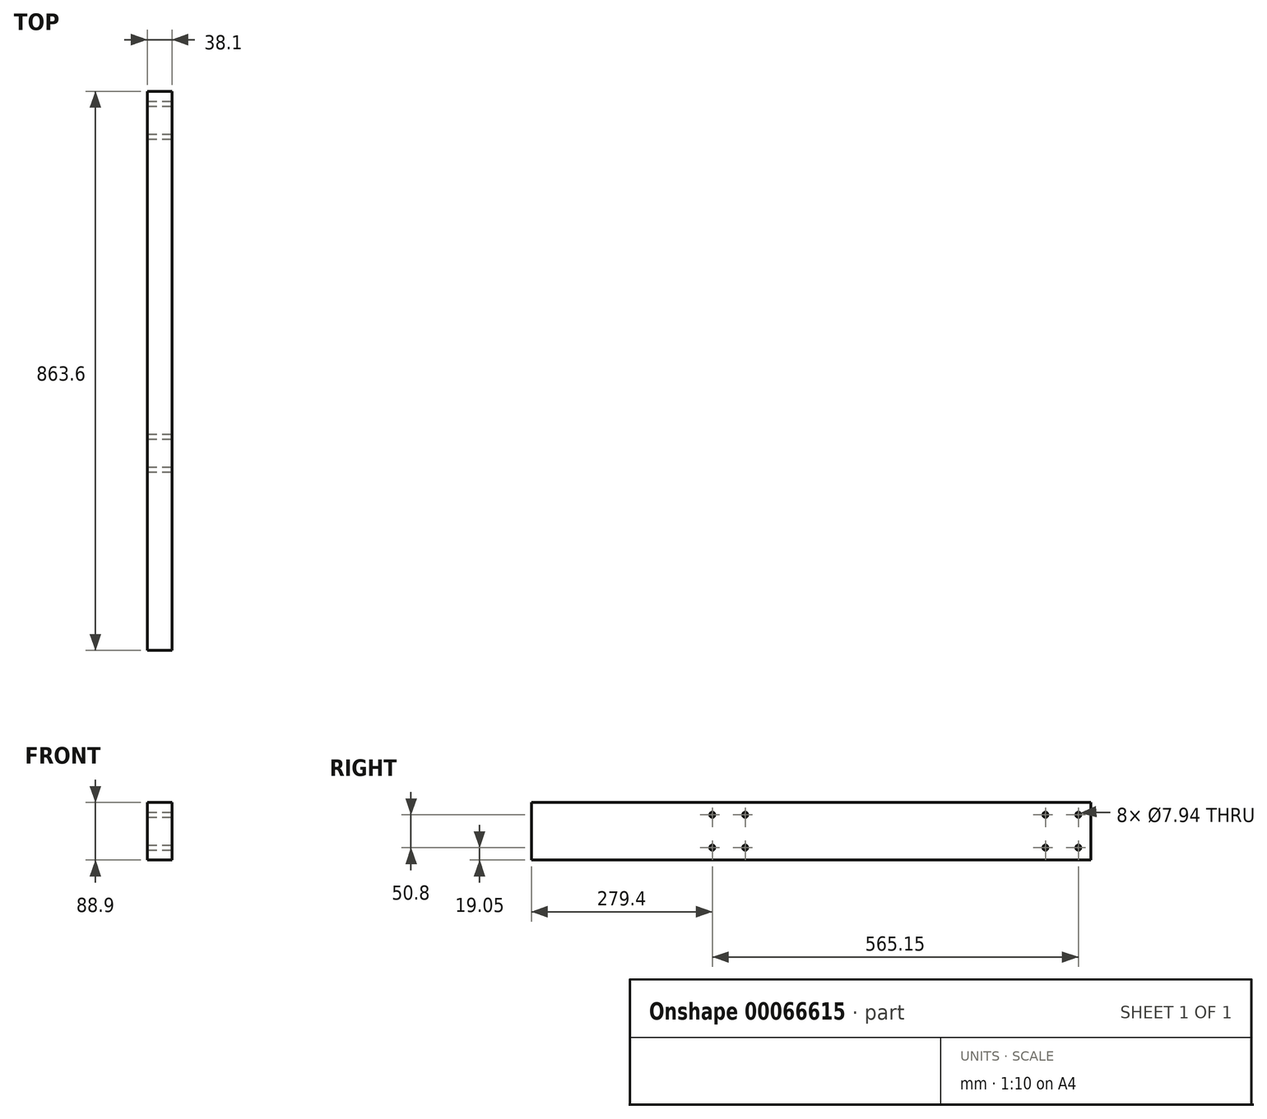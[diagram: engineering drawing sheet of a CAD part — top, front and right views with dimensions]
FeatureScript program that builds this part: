
annotation { "Feature Type Name" : "Feature", "Feature Type Description" : "" }
export const myFeature = defineFeature(function(context is Context, id is Id, definition is map)
    precondition{}
    {
        {
            var Q0;
            Q0=qCreatedBy(makeId("Front.planeOp"),FACE);
            var sketch = newSketch(context, id + "F0", { "sketchPlane" : qUnion([Q0])});
            skLineSegment(sketch, "E0.rect.bottom", {"start": v(19.05, 44.45) * mm, "end": v(-19.05, 44.45) * mm});
            skLineSegment(sketch, "E0.rect.top", {"start": v(19.05, -44.45) * mm, "end": v(-19.05, -44.45) * mm});
            skLineSegment(sketch, "E0.rect.left", {"start": v(19.05, 44.45) * mm, "end": v(19.05, -44.45) * mm});
            skLineSegment(sketch, "E0.rect.right", {"start": v(-19.05, 44.45) * mm, "end": v(-19.05, -44.45) * mm});
            skPoint(sketch, "E0.rect.middle", {"position": v(0, 0) * mm});
            skSolve(sketch);
        }
        {
            var Q0;
            Q0 = qSketchRegion(id + "F0", true);
            extrude(context, id + "F1", {"entities" : qUnion([Q0]), "depth" : 863.6 * mm});
        }
        {
            var Q0;
            Q0=makeQuery(id+"F1.opExtrude","SWEPT_FACE",FACE,{"disambiguationData":[OSD([sQuery(id+"F0.wireOp",EDGE,"E0.rect.left")])]});
            var sketch = newSketch(context, id + "F2", { "sketchPlane" : qUnion([Q0])});
            skLineSegment(sketch, "E1.rect.bottom", {"start": v(0, 44.45) * mm, "end": v(-88.9, 44.45) * mm, "construction": true});
            skLineSegment(sketch, "E1.rect.top", {"start": v(0, -44.45) * mm, "end": v(-88.9, -44.45) * mm, "construction": true});
            skLineSegment(sketch, "E1.rect.left", {"start": v(0, 44.45) * mm, "end": v(0, -44.45) * mm, "construction": true});
            skLineSegment(sketch, "E1.rect.right", {"start": v(-88.9, 44.45) * mm, "end": v(-88.9, -44.45) * mm, "construction": true});
            skPoint(sketch, "E1.rect.middle", {"position": v(-44.45, 0) * mm});
            skLineSegment(sketch, "E2.rect.bottom", {"start": v(-514.35, -44.45) * mm, "end": v(-603.25, -44.45) * mm, "construction": true});
            skLineSegment(sketch, "E2.rect.top", {"start": v(-514.35, 44.45) * mm, "end": v(-603.25, 44.45) * mm, "construction": true});
            skLineSegment(sketch, "E2.rect.left", {"start": v(-514.35, -44.45) * mm, "end": v(-514.35, 44.45) * mm, "construction": true});
            skLineSegment(sketch, "E2.rect.right", {"start": v(-603.25, -44.45) * mm, "end": v(-603.25, 44.45) * mm, "construction": true});
            skPoint(sketch, "E2.rect.middle", {"position": v(-558.8, 0) * mm});
            skLineSegment(sketch, "E3.rect.bottom", {"start": v(-69.85, -25.4) * mm, "end": v(-19.05, -25.4) * mm, "construction": true});
            skLineSegment(sketch, "E3.rect.top", {"start": v(-69.85, 25.4) * mm, "end": v(-19.05, 25.4) * mm, "construction": true});
            skLineSegment(sketch, "E3.rect.left", {"start": v(-69.85, -25.4) * mm, "end": v(-69.85, 25.4) * mm, "construction": true});
            skLineSegment(sketch, "E3.rect.right", {"start": v(-19.05, -25.4) * mm, "end": v(-19.05, 25.4) * mm, "construction": true});
            skLineSegment(sketch, "E4.rect.bottom", {"start": v(-533.4, -25.4) * mm, "end": v(-584.2, -25.4) * mm, "construction": true});
            skLineSegment(sketch, "E4.rect.top", {"start": v(-533.4, 25.4) * mm, "end": v(-584.2, 25.4) * mm, "construction": true});
            skLineSegment(sketch, "E4.rect.left", {"start": v(-533.4, -25.4) * mm, "end": v(-533.4, 25.4) * mm, "construction": true});
            skLineSegment(sketch, "E4.rect.right", {"start": v(-584.2, -25.4) * mm, "end": v(-584.2, 25.4) * mm, "construction": true});
            skCircle(sketch, "E5", {"center": v(-533.4, 25.4) * mm, "radius": 3.97 * mm});
            skCircle(sketch, "E6", {"center": v(-533.4, -25.4) * mm, "radius": 3.97 * mm});
            skCircle(sketch, "E7", {"center": v(-584.2, -25.4) * mm, "radius": 3.97 * mm});
            skCircle(sketch, "E8", {"center": v(-584.2, 25.4) * mm, "radius": 3.97 * mm});
            skCircle(sketch, "E9", {"center": v(-69.85, 25.4) * mm, "radius": 3.97 * mm});
            skCircle(sketch, "E10", {"center": v(-69.85, -25.4) * mm, "radius": 3.97 * mm});
            skCircle(sketch, "E11", {"center": v(-19.05, -25.4) * mm, "radius": 3.97 * mm});
            skCircle(sketch, "E12", {"center": v(-19.05, 25.4) * mm, "radius": 3.97 * mm});
            skSolve(sketch);
        }
        {
            var Q0;
            Q0 = qSketchRegion(id + "F2", true);
            extrude(context, id + "F3", {"entities" : qUnion([Q0]), "operationType" : NewBodyOperationType.REMOVE, "endBound" : BoundingType.THROUGH_ALL, "oppositeDirection" : true, "depth" : 25.4 * mm});
        }
    });
